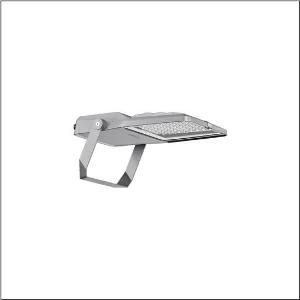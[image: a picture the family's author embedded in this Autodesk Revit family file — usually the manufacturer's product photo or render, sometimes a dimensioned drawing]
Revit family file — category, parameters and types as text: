
# Revit family: floodlight_fl_21_iq_mini___rs12_5xa7772b4b1a_ec65
name_source: partatom
category: Lighting Fixtures
units: mm (PartAtom-declared; Revit-internal decimal feet)

## family parameters
Cut with Voids When Loaded = No
Host = Face
Light Source = No
Part Type = Normal
Room Calculation Point = No
Round Connector Dimension = Use Diameter
Shared = No

## types (1)
- --- (1 x LED, 6560 lm, 45.5 W, 4000K)
    Apparent Load = 46 VA
    CIE Flux Codes = 79 92 99 100 100
    Color Rendering = 70
    Color Temperature = 4000K
    Default Elevation = 1800 mm
    Description = Floodlight FL 21 iQ mini, floodlight, primary light control with lens, of PMMA, primary optical cover: protective disc, of toughened safety glass, transparent, light distribution: RS12, light emission: direct distribution, installation type: surface-mounted, LED, High Power LED, rated luminous flux: 6.560lm, luminous efficacy: 144lm/W, light colour: 740, colour temperature: 4000K, control: Street-Remote, Auto-Match, Temp-Guard, Night-Set, Smart-Wire, Desk-Remote (wireless, voltage-free reading and setting of iQ features in the workshop via application-optimized NFC function/RFID function), optimised constant luminous flux control (CLO 2.0), with terminal, 6-pole, mains connection: 220..240V, AC, 50/60Hz, start of lifetime: 46W, end of service life: 48W, reduction: 22W, luminaire housing, of diecast aluminium, powder-coated, Siteco® metallic grey (DB 702S), corrosivity category C5 mid according to DIN EN ISO 12944, sealing non-destructively replaceable, mounting bracket, of steel, galvanised, powder-coated, Siteco® metallic grey (DB 702S), protection rating (complete): IP66, insulation class (complete): insulation class II (safety insulation), certification: CE, ENEC, VDE, protection symbol: D, impact resistance: IK08, permissible operating ambient temperature: -40..+40°C, permissible operating ambient temperature for outdoor applications: -40..+50°C, standard: DIN EN 12944, LABS conformity tested according to VDMA 24364:2018-05, packaging unit: 1 piece

Light Distribution: RS12
    Height = 70 mm
    Lamp = 1 x LED
    Lamp Light Flux = 6560 lm
    Lamp Power = 45.5 W
    Lamp count = 1
    Length = 485 mm
    Luminous efficacy = 144 lm/W
    Manufacturer = Siteco
    ModVariant = No
    Model = 5XA7772B4B1A
    Number of Poles = 1
    OnlyDefault = Yes
    Power Factor = 1
    Product Name = Floodlight FL 21 iQ mini | RS12
    Product group = floodlight | pylon annexe
    ProductGroupID = 6200
    Protection Class = Protection class II
    Protection Degree = IP 66
    RLX_Detail_Level = 1
    RLX_Emergency_Light_Flux = 0 lm
    RLX_Emergency_Type = 0
    RLX_Emergency_Type_DB = No
    RlxData = <blob elided: 90893 chars, md5=c0148157>
    Socket = socket
    Standby Power = 0 W
    System Light Flux = 6560 lm
    System Power = 46 W
    Type Comments = factory setting: luminous flux: 100 % | dim-lin: 254 | 463 mA
    Type Image = l_1006845.jpg
    URL = http://relux.com
    VarID = @adj_100131
    Voltage = 0 V
    Weight = 0.00 kg
    Width = 337 mm

## geometry (parser evidence)
native form markers: Blend x4, Sweep x13
no freeform markers — native parametric forms only
